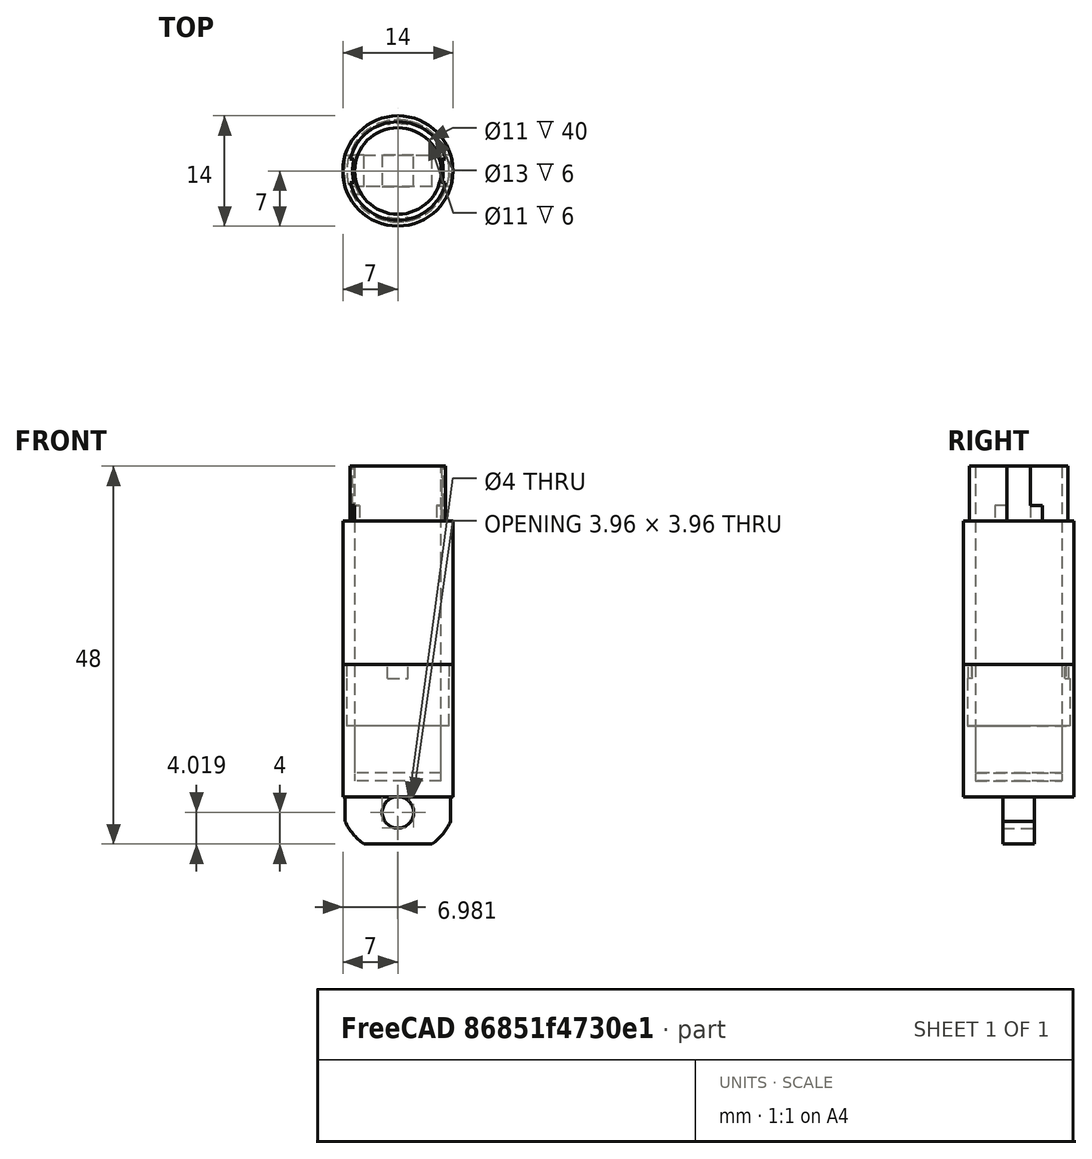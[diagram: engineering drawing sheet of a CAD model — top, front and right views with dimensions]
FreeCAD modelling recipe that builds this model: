
FCSTD DOCUMENT  (FreeCAD 0.20R29177 +233 (Git))
Label: battarey
License: All rights reserved
LicenseURL: http://en.wikipedia.org/wiki/All_rights_reserved
objects: Sketcher::SketchObject×10, PartDesign::Pad×7, PartDesign::Pocket×3, PartDesign::Body×2, Mesh::Feature×2
note: 32 computed .brp shape members not serialized (recipe doc carries the construction recipe); baked Part::Feature solids carry a one-line shape summary decoded from their .brp

FEATURE [Sketcher::SketchObject] Sketch
  FullyConstrained = true
  MapMode = 5
  Support = -> [XY_Plane]
  sketch-geometry (1):
    g0: Circle CenterX=0 CenterY=0 CenterZ=0 NormalX=0 NormalY=0 NormalZ=1 AngleXU=0 Radius=7
  constraints (2):
    c: Coincident(g0,g-1)
    c: Diameter(g0) = 14
FEATURE [PartDesign::Pad] Pad
  Direction = (0,0,1)
  Length = 2
  Length2 = 10
  Profile = -> Sketch
  ReferenceAxis = -> Sketch [N_Axis]
  Type = 0
FEATURE [Sketcher::SketchObject] Sketch001
  ExternalGeometry = -> [Pad]
  FullyConstrained = false
  MapMode = 5
  Placement = pos=(0,0,2) rot=(0,0,1;0rad)
  Support = -> [Pad]
  sketch-geometry (2):
    g0: Circle CenterX=0 CenterY=0 CenterZ=0 NormalX=0 NormalY=0 NormalZ=1 AngleXU=0 Radius=5.5
    g1: Circle CenterX=0 CenterY=0 CenterZ=0 NormalX=0 NormalY=0 NormalZ=1 AngleXU=0 Radius=7
  constraints (3):
    c: Diameter(g0) = 11
    c: Coincident(g1,g0)
    c: Equal(g-3,g1)
FEATURE [PartDesign::Pad] Pad001
  BaseFeature = -> Pad
  Direction = (0,0,1)
  Length = 40
  Length2 = 10
  Profile = -> Sketch001
  ReferenceAxis = -> Sketch001 [N_Axis]
  Type = 0
FEATURE [Sketcher::SketchObject] Sketch002
  ExternalGeometry = -> [Pad001]
  FullyConstrained = true
  MapMode = 5
  Placement = pos=(0,0,42) rot=(0,0,1;0rad)
  Support = -> [Pad001]
  sketch-geometry (9):
    g0: Circle CenterX=0 CenterY=0 CenterZ=0 NormalX=0 NormalY=0 NormalZ=1 AngleXU=0 Radius=7
    g1: ArcOfCircle CenterX=0 CenterY=0 CenterZ=0 NormalX=0 NormalY=0 NormalZ=1 AngleXU=0 Radius=5.75 StartAngle=6.01926 EndAngle=6.54711
    g2: LineSegment StartX=5.5509 StartY=1.5 StartZ=0 EndX=6.06733 EndY=1.5 EndZ=0
    g3: LineSegment StartX=5.5509 StartY=-1.5 StartZ=0 EndX=6.06733 EndY=-1.5 EndZ=0
    g4: ArcOfCircle CenterX=0 CenterY=0 CenterZ=0 NormalX=0 NormalY=0 NormalZ=1 AngleXU=0 Radius=5.75 StartAngle=2.87767 EndAngle=3.40552
    g5: LineSegment StartX=-5.5509 StartY=1.5 StartZ=0 EndX=-6.06733 EndY=1.5 EndZ=0
    g6: LineSegment StartX=-5.5509 StartY=-1.5 StartZ=0 EndX=-6.06733 EndY=-1.5 EndZ=0
    g7: ArcOfCircle CenterX=0 CenterY=0 CenterZ=0 NormalX=0 NormalY=0 NormalZ=1 AngleXU=0 Radius=6.25 StartAngle=0.242366 EndAngle=2.89923
    g8: ArcOfCircle CenterX=0 CenterY=0 CenterZ=0 NormalX=0 NormalY=0 NormalZ=1 AngleXU=0 Radius=6.25 StartAngle=3.38396 EndAngle=6.04082
  constraints (26):
    c: Coincident(g0,g-4)
    c: Coincident(g1,g0)
    c: Diameter(g1) = 11.5
    c: Coincident(g2,g1)
    c: Horizontal(g2)
    c: Coincident(g3,g1)
    c: Horizontal(g3)
    c: Diameter(g4) = 11.5
    c: Coincident(g5,g4)
    c: Horizontal(g5)
    c: Coincident(g6,g4)
    c: Horizontal(g6)
    c: Coincident(g7,g0)
    c: Coincident(g7,g5)
    c: Coincident(g7,g2)
    c: Coincident(g8,g0)
    c: Coincident(g8,g6)
    c: Coincident(g8,g3)
    c: Coincident(g0,g4)
    c: Diameter(g0) = 14
    c: Diameter(g7) = 12.5
    c: Diameter(g8) = 12.5
    c: Distance(g2,g-1) = 1.5
    c: Distance(g3,g-1) = 1.5
    c: Distance(g5,g-1) = 1.5
    c: Distance(g6,g-1) = 1.5
FEATURE [PartDesign::Pocket] Pocket
  BaseFeature = -> Pad001
  Direction = (0,0,-1)
  Length = 5
  Length2 = 5
  Profile = -> Sketch002
  ReferenceAxis = -> Sketch002 [N_Axis]
  Type = 0
FEATURE [Sketcher::SketchObject] Sketch003
  ExternalGeometry = -> [Pad001]
  FullyConstrained = true
  MapMode = 5
  Placement = pos=(0,0,37) rot=(0,0,1;0rad)
  Support = -> [Pocket]
  expr: Constraints[19] = Sketch002.Constraints[19]
  expr: Constraints[20] = Sketch002.Constraints[20]
  expr: Constraints[21] = Sketch002.Constraints[21]
  expr: Constraints[22] = Sketch002.Constraints[23]
  expr: Constraints[23] = Sketch002.Constraints[24]
  expr: Constraints[2] = Sketch002.Constraints[2]
  expr: Constraints[7] = Sketch002.Constraints[7]
  sketch-geometry (9):
    g0: Circle CenterX=0 CenterY=0 CenterZ=0 NormalX=0 NormalY=0 NormalZ=1 AngleXU=0 Radius=7
    g1: ArcOfCircle CenterX=0 CenterY=0 CenterZ=0 NormalX=0 NormalY=0 NormalZ=1 AngleXU=0 Radius=5.75 StartAngle=6.01926 EndAngle=6.83207
    g2: LineSegment StartX=4.90535 StartY=3 StartZ=0 EndX=5.48293 EndY=3 EndZ=0
    g3: LineSegment StartX=5.5509 StartY=-1.5 StartZ=0 EndX=6.06733 EndY=-1.5 EndZ=0
    g4: ArcOfCircle CenterX=0 CenterY=0 CenterZ=0 NormalX=0 NormalY=0 NormalZ=1 AngleXU=0 Radius=5.75 StartAngle=2.87767 EndAngle=3.69048
    g5: LineSegment StartX=-5.5509 StartY=1.5 StartZ=0 EndX=-6.06733 EndY=1.5 EndZ=0
    g6: LineSegment StartX=-4.90535 StartY=-3 StartZ=0 EndX=-5.48293 EndY=-3 EndZ=0
    g7: ArcOfCircle CenterX=0 CenterY=0 CenterZ=0 NormalX=0 NormalY=0 NormalZ=1 AngleXU=0 Radius=6.25 StartAngle=0.500655 EndAngle=2.89923
    g8: ArcOfCircle CenterX=0 CenterY=0 CenterZ=0 NormalX=0 NormalY=0 NormalZ=1 AngleXU=0 Radius=6.25 StartAngle=3.64225 EndAngle=6.04082
  constraints (26):
    c: Coincident(g0,g-4)
    c: Coincident(g1,g0)
    c: Diameter(g1) = 11.5
    c: Coincident(g2,g1)
    c: Horizontal(g2)
    c: Coincident(g3,g1)
    c: Horizontal(g3)
    c: Diameter(g4) = 11.5
    c: Coincident(g5,g4)
    c: Horizontal(g5)
    c: Coincident(g6,g4)
    c: Horizontal(g6)
    c: Coincident(g7,g0)
    c: Coincident(g7,g5)
    c: Coincident(g7,g2)
    c: Coincident(g8,g0)
    c: Coincident(g8,g6)
    c: Coincident(g8,g3)
    c: Coincident(g0,g4)
    c: Diameter(g0) = 14
    c: Diameter(g7) = 12.5
    c: Diameter(g8) = 12.5
    c: Distance(g3,g-1) = 1.5
    c: Distance(g5,g-1) = 1.5
    c: Distance(g2,g-1) = 3
    c: Distance(g6,g-1) = 3
FEATURE [PartDesign::Pocket] Pocket001
  BaseFeature = -> Pocket
  Direction = (0,0,-1)
  Length = 2
  Length2 = 5
  Profile = -> Sketch003
  ReferenceAxis = -> Sketch003 [N_Axis]
  Type = 0
FEATURE [Sketcher::SketchObject] Sketch005
  FullyConstrained = true
  MapMode = 5
  Support = -> [XY_Plane001]
  sketch-geometry (1):
    g0: Circle CenterX=0 CenterY=0 CenterZ=0 NormalX=0 NormalY=0 NormalZ=1 AngleXU=0 Radius=7
  constraints (2):
    c: Coincident(g0,g-1)
    c: Diameter(g0) = 14
FEATURE [PartDesign::Pad] Pad002
  Direction = (0,0,1)
  Length = 3
  Length2 = 10
  Profile = -> Sketch005
  ReferenceAxis = -> Sketch005 [N_Axis]
  Type = 0
FEATURE [Sketcher::SketchObject] Sketch006
  ExternalGeometry = -> [Pad]
  FullyConstrained = false
  MapMode = 5
  Placement = pos=(0,0,3) rot=(0,0,1;0rad)
  Support = -> [Pad002]
  sketch-geometry (2):
    g0: Circle CenterX=0 CenterY=0 CenterZ=0 NormalX=0 NormalY=0 NormalZ=1 AngleXU=0 Radius=5.5
    g1: Circle CenterX=0 CenterY=0 CenterZ=0 NormalX=0 NormalY=0 NormalZ=1 AngleXU=0 Radius=7
  constraints (3):
    c: Diameter(g0) = 11
    c: Coincident(g1,g0)
    c: Equal(g-3,g1)
FEATURE [PartDesign::Pad] Pad003
  BaseFeature = -> Pad002
  Direction = (0,0,1)
  Length = 6
  Length2 = 10
  Profile = -> Sketch006
  ReferenceAxis = -> Sketch006 [N_Axis]
  Type = 0
FEATURE [Sketcher::SketchObject] Sketch008
  FullyConstrained = true
  MapMode = 5
  Placement = pos=(0,0,9) rot=(0,0,1;0rad)
  Support = -> [Pad003]
  sketch-geometry (2):
    g0: Circle CenterX=0 CenterY=0 CenterZ=0 NormalX=0 NormalY=0 NormalZ=1 AngleXU=0 Radius=7
    g1: Circle CenterX=0 CenterY=0 CenterZ=0 NormalX=0 NormalY=0 NormalZ=1 AngleXU=0 Radius=6.5
  constraints (4):
    c: Coincident(g0,g-1)
    c: Coincident(g1,g0)
    c: Diameter(g1) = 13
    c: Diameter(g0) = 14
FEATURE [PartDesign::Pad] Pad004
  BaseFeature = -> Pad003
  Direction = (0,0,1)
  Length = 6
  Length2 = 10
  Profile = -> Sketch008
  ReferenceAxis = -> Sketch008 [N_Axis]
  Type = 0
FEATURE [Sketcher::SketchObject] Sketch007
  ExternalGeometry = -> [Pad001]
  FullyConstrained = true
  MapMode = 11
  Placement = pos=(0,0,15) rot=(0,0,1;1.5708rad)
  Support = -> [Pad004]
  sketch-geometry (9):
    g0: Circle CenterX=0 CenterY=0 CenterZ=0 NormalX=0 NormalY=0 NormalZ=1 AngleXU=0 Radius=7
    g1: ArcOfCircle CenterX=0 CenterY=0 CenterZ=0 NormalX=0 NormalY=0 NormalZ=1 AngleXU=0 Radius=6 StartAngle=6.06479 EndAngle=6.50158
    g2: LineSegment StartX=5.85747 StartY=1.3 StartZ=0 EndX=6.36867 EndY=1.3 EndZ=0
    g3: LineSegment StartX=5.85747 StartY=-1.3 StartZ=0 EndX=6.36867 EndY=-1.3 EndZ=0
    g4: ArcOfCircle CenterX=0 CenterY=0 CenterZ=0 NormalX=0 NormalY=0 NormalZ=1 AngleXU=0 Radius=6 StartAngle=2.92319 EndAngle=3.35999
    g5: LineSegment StartX=-5.85747 StartY=1.3 StartZ=0 EndX=-6.36867 EndY=1.3 EndZ=0
    g6: LineSegment StartX=-5.85747 StartY=-1.3 StartZ=0 EndX=-6.36867 EndY=-1.3 EndZ=0
    g7: ArcOfCircle CenterX=0 CenterY=0 CenterZ=0 NormalX=0 NormalY=0 NormalZ=1 AngleXU=0 Radius=6.5 StartAngle=0.201358 EndAngle=2.94023
    g8: ArcOfCircle CenterX=0 CenterY=0 CenterZ=0 NormalX=0 NormalY=0 NormalZ=1 AngleXU=0 Radius=6.5 StartAngle=3.34295 EndAngle=6.08183
  constraints (26):
    c: Coincident(g0,g-4)
    c: Coincident(g1,g0)
    c: Diameter(g1) = 12
    c: Coincident(g2,g1)
    c: Horizontal(g2)
    c: Coincident(g3,g1)
    c: Horizontal(g3)
    c: Diameter(g4) = 12
    c: Coincident(g5,g4)
    c: Horizontal(g5)
    c: Coincident(g6,g4)
    c: Horizontal(g6)
    c: Coincident(g7,g0)
    c: Coincident(g7,g5)
    c: Coincident(g7,g2)
    c: Coincident(g8,g0)
    c: Coincident(g8,g6)
    c: Coincident(g8,g3)
    c: Coincident(g0,g4)
    c: Diameter(g0) = 14
    c: Diameter(g7) = 13
    c: Diameter(g8) = 13
    c: Distance(g2,g-1) = 1.3
    c: Distance(g3,g-1) = 1.3
    c: Distance(g5,g-1) = 1.3
    c: Distance(g6,g-1) = 1.3
FEATURE [PartDesign::Pad] Pad005
  BaseFeature = -> Pad004
  Direction = (0,0,1)
  Length = 1.8
  Length2 = 10
  Profile = -> Sketch007
  ReferenceAxis = -> Sketch007 [N_Axis]
  Type = 0
FEATURE [PartDesign::Body] Body001
  Group = -> [Sketch005,Sketch006,Sketch007,Sketch008,Pad002,Pad003,Pad004,Pad005]
  Origin = -> Origin001
  Tip = -> Pad005
FEATURE [Sketcher::SketchObject] Sketch009
  ExternalGeometry = -> [Pocket001]
  FullyConstrained = true
  MapMode = 5
  Placement = pos=(0,0,0) rot=(1,0,0;3.14159rad)
  Support = -> [Pocket001]
  sketch-geometry (5):
    g0: LineSegment StartX=-6.7082 StartY=2 StartZ=0 EndX=-6.7082 EndY=-2 EndZ=0
    g1: LineSegment StartX=-6.7082 StartY=-2 StartZ=0 EndX=6.7082 EndY=-2 EndZ=0
    g2: LineSegment StartX=6.7082 StartY=-2 StartZ=0 EndX=6.7082 EndY=2 EndZ=0
    g3: LineSegment StartX=6.7082 StartY=2 StartZ=0 EndX=-6.7082 EndY=2 EndZ=0
    g4: GeomPoint X=0 Y=0 Z=0
  constraints (12):
    c: Coincident(g0,g1)
    c: Coincident(g1,g2)
    c: Coincident(g2,g3)
    c: Coincident(g3,g0)
    c: Horizontal(g1)
    c: Horizontal(g3)
    c: Vertical(g0)
    c: Vertical(g2)
    c: Symmetric(g1,g0,g4)
    c: Coincident(g4,g-3)
    c: PointOnObject(g1,g-3)
    c: DistanceY(g2,g2) = 4
FEATURE [PartDesign::Pad] Pad006
  BaseFeature = -> Pocket001
  Direction = (0,0,-1)
  Length = 6
  Length2 = 10
  Profile = -> Sketch009
  ReferenceAxis = -> Sketch009 [N_Axis]
  Type = 0
FEATURE [Sketcher::SketchObject] Sketch010
  ExternalGeometry = -> [Pad006]
  FullyConstrained = false
  MapMode = 5
  Placement = pos=(0,2,0) rot=(0,0.707107,0.707107;3.14159rad)
  Support = -> [Pad006]
  sketch-geometry (5):
    g0: ArcOfCircle CenterX=0 CenterY=0 CenterZ=0 NormalX=0 NormalY=0 NormalZ=1 AngleXU=0 Radius=7.40007 StartAngle=3.57746 EndAngle=5.84732
    g1: Circle CenterX=0 CenterY=-2 CenterZ=0 NormalX=0 NormalY=0 NormalZ=1 AngleXU=0 Radius=2
    g2: LineSegment StartX=-6.7082 StartY=-3.12427 StartZ=0 EndX=-6.7082 EndY=-8.22579 EndZ=0
    g3: LineSegment StartX=-6.7082 StartY=-8.22579 StartZ=0 EndX=7.52102 EndY=-8.22579 EndZ=0
    g4: LineSegment StartX=7.52102 StartY=-8.22579 StartZ=0 EndX=6.7082 EndY=-3.12427 EndZ=0
  constraints (12):
    c: Coincident(g0,g-1)
    c: PointOnObject(g0,g-3)
    c: PointOnObject(g0,g-4)
    c: PointOnObject(g1,g-2)
    c: PointOnObject(g0,g1)
    c: Diameter(g1) = 4
    c: Coincident(g2,g0)
    c: Vertical(g2)
    c: Coincident(g3,g2)
    c: Horizontal(g3)
    c: Coincident(g4,g3)
    c: Coincident(g4,g0)
FEATURE [PartDesign::Pocket] Pocket002
  BaseFeature = -> Pad006
  Direction = (0,-1,2e-16)
  Length = 5
  Length2 = 5
  Profile = -> Sketch010
  ReferenceAxis = -> Sketch010 [N_Axis]
  Type = 0
FEATURE [PartDesign::Body] Body
  Group = -> [Sketch,Pad,Sketch001,Pad001,Sketch002,Pocket,Sketch003,Pocket001,Sketch009,Pad006,Sketch010,Pocket002]
  Origin = -> Origin
  Tip = -> Pocket002
FEATURE [Mesh::Feature] Mesh  label="Body (Meshed)"
FEATURE [Mesh::Feature] Mesh001  label="Body001 (Meshed)"
